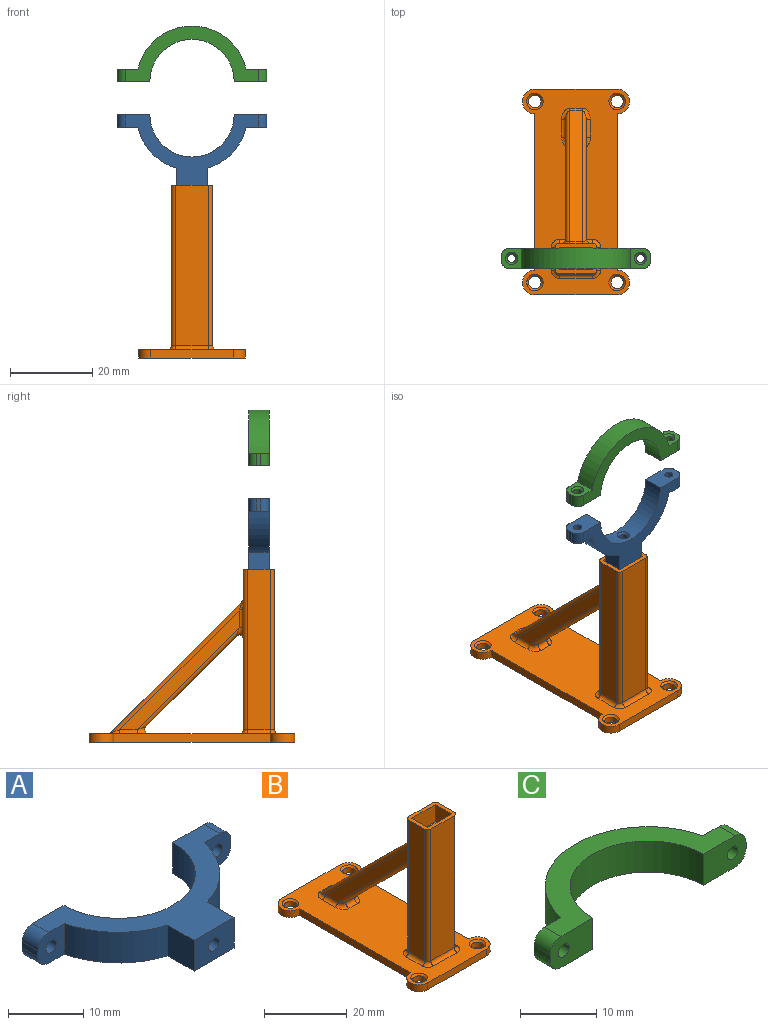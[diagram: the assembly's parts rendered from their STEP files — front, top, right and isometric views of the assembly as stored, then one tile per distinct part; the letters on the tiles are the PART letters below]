
ASSEMBLY  parts=3 mates=2
PART A: 22 faces, bbox 36.3x18x5 mm
  f0: cylinder r=10.25mm len=20.5mm, axis (0,0,-1), area 154.3mm2, adj f10,f11,f15,f20,f21
  f1: plane 5x5mm, normal (0,-1,0), area 20.1mm2, adj f2,f9,f10,f11,f13,f16,f18
  f2: cylinder r=13.5mm len=9.98mm, axis (0,0,-1), area 72mm2, adj f1,f3,f10,f11
  f3: plane 5.02x5mm, normal (-1,0,0), area 25.1mm2, adj f2,f4,f10,f11
  f4: plane 7.5x5mm, normal (0,-1,0), area 34.4mm2, adj f3,f5,f10,f11,f12
  f5: plane 5.04x5mm, normal (1,0,0), area 25.2mm2, adj f4,f6,f10,f11
  f6: cylinder r=13.5mm len=9.96mm, axis (0,0,-1), area 71.8mm2, adj f5,f7,f10,f11
  f7: plane 5x5mm, normal (0,-1,0), area 20.1mm2, adj f6,f8,f10,f11,f14,f17,f19
  f8: plane 3x1mm, normal (1,0,0), area 3mm2, adj f7,f17,f19,f20
  f9: plane 3x1mm, normal (-1,0,0), area 3mm2, adj f1,f16,f18,f21
  f10: plane 32.33x18mm, normal (0,0,1), area 173mm2, adj f0,f1,f2,f3,f4,f5,f6,f7
  f11: plane 32.33x18mm, normal (0,0,-1), area 173mm2, adj f0,f1,f2,f3,f4,f5,f6,f7
  f12: cylinder r=1mm len=7.25mm, axis (0,-1,0), area 45.6mm2, adj f4,f15
  f13: cylinder r=1mm len=3mm, axis (0,1,0), area 18.8mm2, adj f1,f21
  f14: cylinder r=1mm len=3mm, axis (0,1,0), area 18.8mm2, adj f7,f20
  f15: bspline ~3x2.86mm, area 5.3mm2, adj f0,f12
  f16: cylinder r=2mm len=3mm, axis (0,-1,0), area 9.4mm2, adj f1,f9,f11,f21
  f17: cylinder r=2mm len=3mm, axis (0,1,0), area 9.4mm2, adj f7,f8,f11,f20
  f18: cylinder r=2mm len=3mm, axis (0,1,0), area 9.4mm2, adj f1,f9,f10,f21
  f19: cylinder r=2mm len=3mm, axis (0,-1,0), area 9.4mm2, adj f7,f8,f10,f20
  f20: plane 7.91x5mm, normal (0,1,0), area 34.7mm2, adj f0,f8,f10,f11,f14,f17,f19
  f21: plane 7.91x5mm, normal (0,1,0), area 34.7mm2, adj f0,f9,f10,f11,f13,f16,f18
PART B: 66 faces, bbox 26x50x42 mm
  f0: plane 50x26mm, normal (0,0,1), area 831.3mm2, adj f5,f6,f7,f8,f9,f10,f11,f16
  f1: plane 39x8mm, normal (0,1,0), area 247.6mm2, adj f2,f38,f39,f42,f43,f46,f47,f48
  f2: plane 10x7.5mm, normal (0,0,1), area 30.1mm2, adj f1,f18,f19,f20,f23,f24,f25,f26
  f3: plane 29.09x29.09mm, normal (-1,0,0), area 114.4mm2, adj f36,f37,f45,f46
  f4: plane 29.09x29.09mm, normal (1,0,0), area 114.4mm2, adj f33,f34,f43,f44
  f5: cylinder r=3mm len=6mm, axis (0,0,-1), area 18.8mm2, adj f0,f6,f16,f17
  f6: plane 38x2mm, normal (-1,0,0), area 76mm2, adj f0,f5,f7,f17
  f7: cylinder r=3mm len=6mm, axis (0,0,-1), area 18.8mm2, adj f0,f6,f8,f17
  f8: plane 20x2mm, normal (0,-1,0), area 40mm2, adj f0,f7,f9,f17
  f9: cylinder r=3mm len=6mm, axis (0,0,-1), area 18.8mm2, adj f0,f8,f10,f17
  f10: plane 38x2mm, normal (1,0,0), area 76mm2, adj f0,f9,f11,f17
  f11: cylinder r=3mm len=6mm, axis (0,0,-1), area 18.8mm2, adj f0,f10,f16,f17
  f12: cylinder r=1.5mm len=3mm, axis (0,0,-1), area 14.1mm2, adj f17,f64
  f13: cylinder r=1.5mm len=3mm, axis (0,0,-1), area 14.1mm2, adj f17,f63
  f14: cylinder r=1.5mm len=3mm, axis (0,0,-1), area 14.1mm2, adj f17,f65
  f15: cylinder r=1.5mm len=3mm, axis (0,0,-1), area 14.1mm2, adj f17,f62
  f16: plane 20x2mm, normal (0,1,0), area 40mm2, adj f0,f5,f11,f17
  f17: plane 50x26mm, normal (0,0,-1), area 1028.3mm2, adj f5,f6,f7,f8,f9,f10,f11,f12
  f18: plane 39x5.5mm, normal (1,0,0), area 214.5mm2, adj f2,f55,f58,f61
  f19: plane 39x5.5mm, normal (-1,0,0), area 214.5mm2, adj f2,f50,f51,f52
  f20: plane 39x8mm, normal (0,-1,0), area 312mm2, adj f2,f52,f57,f58
  f21: plane 31.91x31.91mm, normal (0,0.71,0.71), area 135.4mm2, adj f30,f33,f37,f38
  f22: plane 22.01x22.01mm, normal (0,-0.71,-0.71), area 93.4mm2, adj f35,f44,f45,f49
  f23: plane 5.5x5mm, normal (1,0,0), area 27.5mm2, adj f2,f24,f26,f27
  f24: plane 8x5mm, normal (0,1,0), area 40mm2, adj f2,f23,f25,f27
  f25: plane 5.5x5mm, normal (-1,0,0), area 27.5mm2, adj f2,f24,f26,f27
  f26: plane 8x5mm, normal (0,-1,0), area 40mm2, adj f2,f23,f25,f27
  f27: plane 8x5.5mm, normal (0,0,1), area 40.9mm2, adj f23,f24,f25,f26,f28
  f28: cylinder r=1mm len=7mm, axis (0,0,1), area 44mm2, adj f27,f29
  f29: plane 2x2mm, normal (0,0,1), area 3.1mm2, adj f28
  f30: cylinder r=1mm len=3mm, axis (-1,0,0), area 2.4mm2, adj f0,f21,f31,f32
  f31: bspline ~3.32x2.09mm, area 3.5mm2, adj f0,f30,f33,f34
  f32: bspline ~3.32x2mm, area 3.5mm2, adj f0,f30,f36,f37
  f33: cylinder r=1mm len=32.62mm, axis (0,-0.71,0.71), area 68.6mm2, adj f4,f21,f31,f39
  f34: cylinder r=1mm len=4.24mm, axis (0,1,0), area 6.7mm2, adj f0,f4,f31,f40
  f35: cylinder r=1mm len=3mm, axis (1,0,0), area 7.1mm2, adj f0,f22,f40,f41
  f36: cylinder r=1mm len=4.24mm, axis (0,-1,0), area 6.7mm2, adj f0,f3,f32,f41
  f37: cylinder r=1mm len=32.62mm, axis (0,0.71,-0.71), area 68.6mm2, adj f3,f21,f32,f42
  f38: cylinder r=1mm len=3mm, axis (1,0,0), area 2.4mm2, adj f1,f21,f39,f42
  f39: bspline ~2.83x2mm, area 3.5mm2, adj f1,f33,f38,f43
  f40: bspline ~3.32x2.35mm, area 5.4mm2, adj f0,f34,f35,f44
  f41: bspline ~3.32x2.35mm, area 5.4mm2, adj f0,f35,f36,f45
  f42: bspline ~3.32x2.35mm, area 3.5mm2, adj f1,f37,f38,f46
  f43: cylinder r=1mm len=4.24mm, axis (0,0,1), area 6.7mm2, adj f1,f4,f39,f47
  f44: cylinder r=1mm len=25.55mm, axis (0,0.71,-0.71), area 51.2mm2, adj f4,f22,f40,f47
  f45: cylinder r=1mm len=25.55mm, axis (0,-0.71,0.71), area 51.2mm2, adj f3,f22,f41,f48
  f46: cylinder r=1mm len=4.24mm, axis (0,0,-1), area 6.7mm2, adj f1,f3,f42,f48
  f47: bspline ~3.32x2.35mm, area 5.4mm2, adj f1,f43,f44,f49
  f48: bspline ~3.32x2.35mm, area 5.4mm2, adj f1,f45,f46,f49
  f49: cylinder r=1mm len=3mm, axis (-1,0,0), area 7.1mm2, adj f1,f22,f47,f48
  f50: cylinder r=1mm len=39mm, axis (0,0,-1), area 61.3mm2, adj f1,f2,f19,f53
  f51: cylinder r=1mm len=5.5mm, axis (0,-1,0), area 8.6mm2, adj f0,f19,f53,f54
  f52: cylinder r=1mm len=39mm, axis (0,0,1), area 61.3mm2, adj f2,f19,f20,f54
  f53: torus R=2mm, axis (0,0,1), area 3.4mm2, adj f0,f50,f51,f56
  f54: torus R=2mm, axis (0,0,1), area 3.4mm2, adj f0,f51,f52,f57
  f55: cylinder r=1mm len=39mm, axis (0,0,1), area 61.3mm2, adj f1,f2,f18,f59
  f56: cylinder r=1mm len=8mm, axis (-1,0,0), area 12.6mm2, adj f0,f1,f53,f59
  f57: cylinder r=1mm len=8mm, axis (1,0,0), area 12.6mm2, adj f0,f20,f54,f60
  f58: cylinder r=1mm len=39mm, axis (0,0,-1), area 61.3mm2, adj f2,f18,f20,f60
  f59: torus R=2mm, axis (0,0,1), area 3.4mm2, adj f0,f55,f56,f61
  f60: torus R=2mm, axis (0,0,1), area 3.4mm2, adj f0,f57,f58,f61
  f61: cylinder r=1mm len=5.5mm, axis (0,1,0), area 8.6mm2, adj f0,f18,f59,f60
  f62: cone r=1.5mm half-angle=45deg, axis (0,0,1), area 7.8mm2, adj f0,f15
  f63: cone r=1.5mm half-angle=45deg, axis (0,0,1), area 7.8mm2, adj f0,f13
  f64: cone r=1.5mm half-angle=45deg, axis (0,0,1), area 7.8mm2, adj f0,f12
  f65: cone r=1.5mm half-angle=45deg, axis (0,0,1), area 7.8mm2, adj f0,f14
PART C: 18 faces, bbox 36.3x13.5x5 mm
  f0: plane 3x1mm, normal (1,0,0), area 3mm2, adj f8,f10,f11,f16
  f1: plane 3x1mm, normal (-1,0,0), area 3mm2, adj f7,f9,f13,f17
  f2: cylinder r=10.25mm len=20.5mm, axis (0,0,-1), area 161mm2, adj f3,f4,f16,f17
  f3: plane 32.33x13.5mm, normal (0,0,1), area 137.9mm2, adj f2,f9,f10,f11,f12,f13,f16,f17
  f4: plane 32.33x13.5mm, normal (0,0,-1), area 137.9mm2, adj f2,f7,f8,f11,f12,f13,f16,f17
  f5: cylinder r=1mm len=2.5mm, axis (0,1,0), area 15.7mm2, adj f15,f17
  f6: cylinder r=1mm len=2.5mm, axis (0,1,0), area 15.7mm2, adj f14,f16
  f7: cylinder r=2mm len=3mm, axis (0,-1,0), area 9.4mm2, adj f1,f4,f13,f17
  f8: cylinder r=2mm len=3mm, axis (0,1,0), area 9.4mm2, adj f0,f4,f11,f16
  f9: cylinder r=2mm len=3mm, axis (0,1,0), area 9.4mm2, adj f1,f3,f13,f17
  f10: cylinder r=2mm len=3mm, axis (0,-1,0), area 9.4mm2, adj f0,f3,f11,f16
  f11: plane 5x5mm, normal (0,1,0), area 16.2mm2, adj f0,f3,f4,f8,f10,f12,f14
  f12: cylinder r=13.5mm len=26.33mm, axis (0,0,-1), area 181.8mm2, adj f3,f4,f11,f13
  f13: plane 5x5mm, normal (0,1,0), area 16.2mm2, adj f1,f3,f4,f7,f9,f12,f15
  f14: cone r=1mm half-angle=45deg, axis (0,1,0), area 5.6mm2, adj f6,f11
  f15: cone r=1mm half-angle=45deg, axis (0,1,0), area 5.6mm2, adj f5,f13
  f16: plane 7.91x5mm, normal (0,-1,0), area 34.7mm2, adj f0,f2,f3,f4,f6,f8,f10
  f17: plane 7.91x5mm, normal (0,-1,0), area 34.7mm2, adj f1,f2,f3,f4,f5,f7,f9
PLACE A rot(axis=(1,0,0),90deg) t=(-17.95,-8.97,60.81)mm
PLACE B t=(-17.95,4.78,1.71)mm
PLACE C rot(axis=(1,0,0),90deg) t=(-17.95,-8.97,68.91)mm
MATE slider A.f12 <-> B.f28  axis (0,0,-1) through (-17.95,-11.47,42.81)mm
MATE slider C.f5 <-> A.f13  axis (0,0,1) through (-33.61,-11.47,68.91)mm
